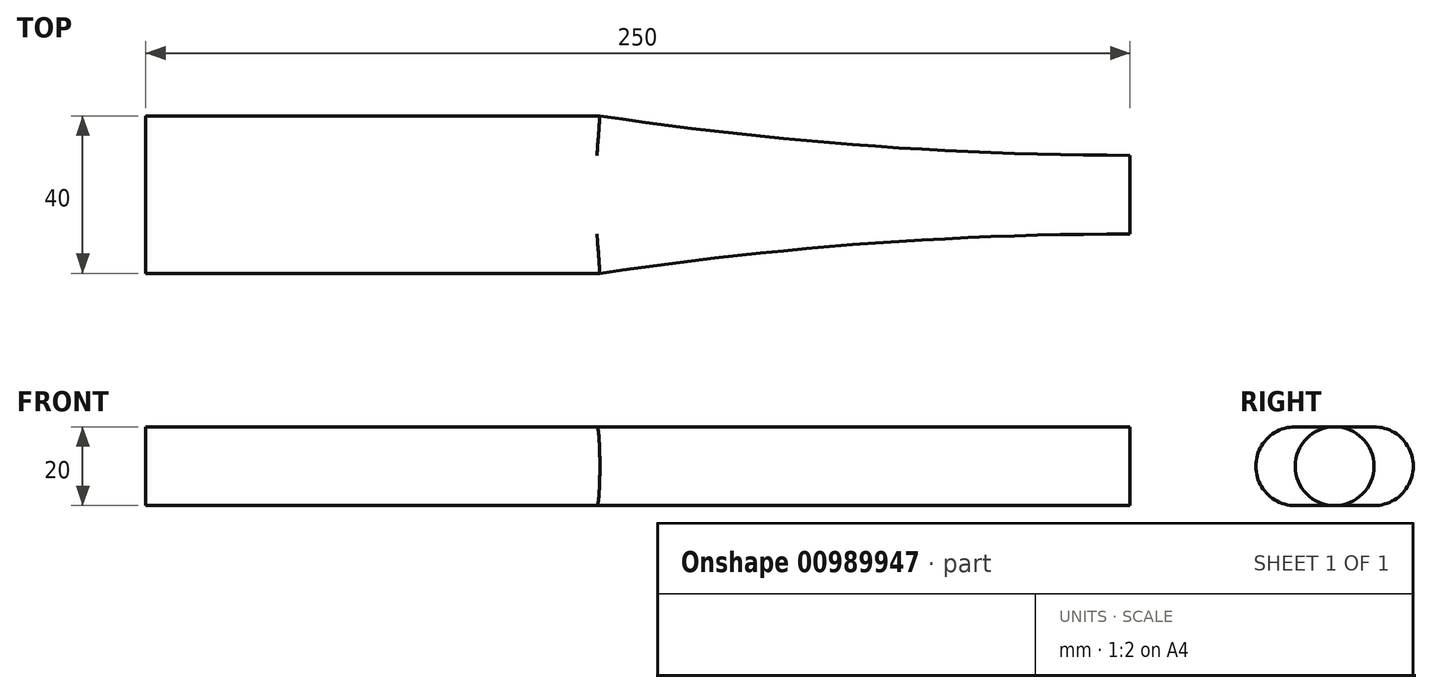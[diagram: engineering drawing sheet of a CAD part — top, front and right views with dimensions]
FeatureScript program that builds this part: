
annotation { "Feature Type Name" : "Feature", "Feature Type Description" : "" }
export const myFeature = defineFeature(function(context is Context, id is Id, definition is map)
    precondition{}
    {
        {
            var Q0;
            Q0=qCreatedBy(makeId("Top.planeOp"),FACE);
            var sketch = newSketch(context, id + "F0", { "sketchPlane" : qUnion([Q0])});
            skLineSegment(sketch, "E0.bottom", {"start": v(0, 0) * mm, "end": v(250, 0) * mm});
            skLineSegment(sketch, "E0.top", {"start": v(0, 20) * mm, "end": v(115.35, 20) * mm});
            skLineSegment(sketch, "E0.left", {"start": v(0, 0) * mm, "end": v(0, 20) * mm});
            skLineSegment(sketch, "E0.right", {"start": v(250, 0) * mm, "end": v(250, 10) * mm});
            skArc(sketch, "E1", {"start": v(115.35, 20) * mm, "mid": v(182.49, 12.5) * mm, "end": v(250, 10) * mm});
            skPoint(sketch, "E2.orphan", {"position": v(250, 20) * mm});
            skSolve(sketch);
        }
        {
            var Q0;
            Q0 = qSketchRegion(id + "F0", true);
            extrude(context, id + "F1", {"entities" : qUnion([Q0]), "depth" : 10 * mm, "offsetDistance" : 25 * mm});
        }
        {
            var Q0;
            Q0=makeQuery(id+"F1.opExtrude","SWEPT_BODY",BODY,{"disambiguationData":[OSD([sQuery(id+"F0.wireOp",EDGE,"E0.bottom"),sQuery(id+"F0.wireOp",EDGE,"E0.top"),sQuery(id+"F0.wireOp",EDGE,"E0.left"),sQuery(id+"F0.wireOp",EDGE,"E0.right"),sQuery(id+"F0.wireOp",EDGE,"E1")])]});
            var Q1;
            Q1=qCreatedBy(makeId("Top.planeOp"),FACE);
            mirror(context, id + "F2", {"operationType" : NewBodyOperationType.ADD, "entities" : qUnion([Q0]), "mirrorPlane" : qUnion([Q1])});
        }
        {
            var Q0;
            Q0=makeQuery(id+"F1.opExtrude","SWEPT_BODY",BODY,{"disambiguationData":[OSD([sQuery(id+"F0.wireOp",EDGE,"E0.bottom"),sQuery(id+"F0.wireOp",EDGE,"E0.top"),sQuery(id+"F0.wireOp",EDGE,"E0.left"),sQuery(id+"F0.wireOp",EDGE,"E0.right"),sQuery(id+"F0.wireOp",EDGE,"E1")])]});
            var Q1;
            Q1=qCreatedBy(makeId("Front.planeOp"),FACE);
            mirror(context, id + "F3", {"operationType" : NewBodyOperationType.ADD, "entities" : qUnion([Q0]), "mirrorPlane" : qUnion([Q1])});
        }
        {
            var Q0;
            Q0=makeQuery(id+"F1.opExtrude","CAP_EDGE",EDGE,{"disambiguationData":[OSD([sQuery(id+"F0.wireOp",EDGE,"E0.top")])],"isStart":false});
            var Q1;
            Q1=makeQuery(id+"F2.opPattern","COPY",EDGE,{"derivedFrom":makeQuery(id+"F1.opExtrude","CAP_EDGE",EDGE,{"disambiguationData":[OSD([sQuery(id+"F0.wireOp",EDGE,"E0.top")])],"isStart":false}),"instanceName":"1"});
            var Q2;
            Q2=makeQuery(id+"F3.opPattern","COPY",EDGE,{"derivedFrom":makeQuery(id+"F1.opExtrude","CAP_EDGE",EDGE,{"disambiguationData":[OSD([sQuery(id+"F0.wireOp",EDGE,"E0.top")])],"isStart":false}),"instanceName":"1"});
            var Q3;
            Q3=makeQuery(id+"F1.opExtrude","CAP_EDGE",EDGE,{"disambiguationData":[OSD([sQuery(id+"F0.wireOp",EDGE,"E1")])],"isStart":false});
            var Q4;
            Q4=makeQuery(id+"F3.opPattern","COPY",EDGE,{"derivedFrom":makeQuery(id+"F1.opExtrude","CAP_EDGE",EDGE,{"disambiguationData":[OSD([sQuery(id+"F0.wireOp",EDGE,"E1")])],"isStart":false}),"instanceName":"1"});
            var Q5;
            Q5=makeQuery(id+"F2.opPattern","COPY",EDGE,{"derivedFrom":makeQuery(id+"F1.opExtrude","CAP_EDGE",EDGE,{"disambiguationData":[OSD([sQuery(id+"F0.wireOp",EDGE,"E1")])],"isStart":false}),"instanceName":"1"});
            var Q6;
            Q6=makeQuery(id+"F3.opPattern","COPY",EDGE,{"derivedFrom":makeQuery(id+"F2.opPattern","COPY",EDGE,{"derivedFrom":makeQuery(id+"F1.opExtrude","CAP_EDGE",EDGE,{"disambiguationData":[OSD([sQuery(id+"F0.wireOp",EDGE,"E0.top")])],"isStart":false}),"instanceName":"1"}),"instanceName":"1"});
            var Q7;
            Q7=makeQuery(id+"F3.opPattern","COPY",EDGE,{"derivedFrom":makeQuery(id+"F2.opPattern","COPY",EDGE,{"derivedFrom":makeQuery(id+"F1.opExtrude","CAP_EDGE",EDGE,{"disambiguationData":[OSD([sQuery(id+"F0.wireOp",EDGE,"E1")])],"isStart":false}),"instanceName":"1"}),"instanceName":"1"});
            fillet(context, id + "F4", {"entities" : qUnion([Q0, Q1, Q2, Q3, Q4, Q5, Q6, Q7]), "tangentPropagation" : true, "radius" : 10 * mm, "defaultsChanged" : true, "vertexSettings" : [], "allowEdgeOverflow" : false});
        }
    });
